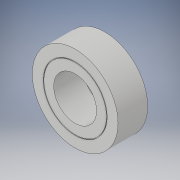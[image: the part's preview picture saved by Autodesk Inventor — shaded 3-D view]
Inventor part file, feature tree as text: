
AUTODESK INVENTOR PART (.ipt)
format: ipt  version: 2018 (Build 220112000, 112)  size: 117,248 bytes
history: native  units: in
note: dims shown in document units (in); Inventor stores cm internally (conversion verified against a paired STEP export)
features: extrude x2, sketch x2
ambient origin geometry x8: Origin, YZ Plane, XZ Plane, XY Plane, X Axis, Y Axis, Z Axis, Center Point
bodies: Body1 (feature_tree)
feature tree (4):
  extrude  "Extrusion2"  Depth=0.65in
  extrude  "Extrusion3"  Depth=0.01in
  sketch  "Sketch1"  dims[d0=1.3in d3=0.65in]
  sketch  "Sketch2"  dims[d4=0.45in d5=0.0in d6=0.01in d8=0.15in d9=0.01in d10=0.0in]
